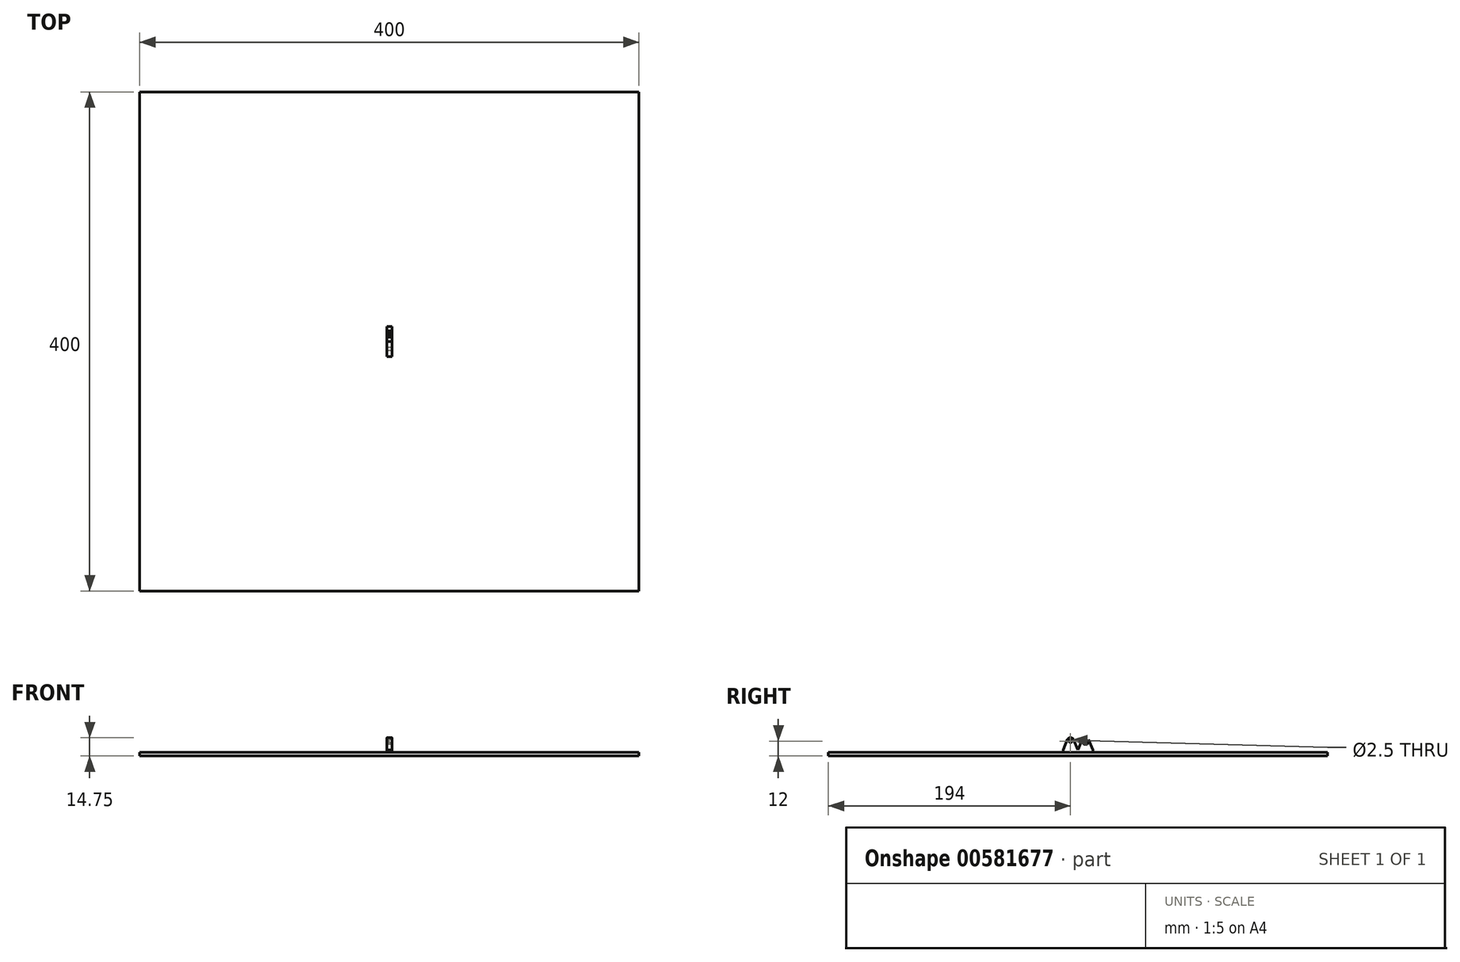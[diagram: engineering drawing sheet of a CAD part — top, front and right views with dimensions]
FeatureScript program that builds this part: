
annotation { "Feature Type Name" : "Feature", "Feature Type Description" : "" }
export const myFeature = defineFeature(function(context is Context, id is Id, definition is map)
    precondition{}
    {
        {
            var Q0;
            Q0=qCreatedBy(makeId("Top.planeOp"),FACE);
            var sketch = newSketch(context, id + "F0", { "sketchPlane" : qUnion([Q0])});
            skLineSegment(sketch, "E0.bottom", {"start": v(-200, -200) * mm, "end": v(200, -200) * mm});
            skLineSegment(sketch, "E0.top", {"start": v(-200, 200) * mm, "end": v(200, 200) * mm});
            skLineSegment(sketch, "E0.left", {"start": v(-200, -200) * mm, "end": v(-200, 200) * mm});
            skLineSegment(sketch, "E0.right", {"start": v(200, -200) * mm, "end": v(200, 200) * mm});
            skPoint(sketch, "E1.firstSnap0", {"position": v(-200, 0) * mm});
            skSolve(sketch);
        }
        {
            var Q0;
            Q0=makeQuery(id+"F0.imprint","IMPRINT",FACE,{"disambiguationData":[TD([[makeQuery(id+"F0.imprint","IMPRINT",EDGE,{"derivedFrom":sQuery(id+"F0.wireOp",EDGE,"E0.bottom")}),1.0]])]});
            extrude(context, id + "F1", {"entities" : qUnion([Q0]), "oppositeDirection" : true, "depth" : 3 * mm, "offsetDistance" : 25 * mm});
        }
        {
            var Q0;
            Q0=qCreatedBy(makeId("Right.planeOp"),FACE);
            var sketch = newSketch(context, id + "F2", { "sketchPlane" : qUnion([Q0])});
            skLineSegment(sketch, "E2.bottom", {"start": v(-12, 0) * mm, "end": v(0, 0) * mm});
            skLineSegment(sketch, "E2.top", {"start": v(-12, 2) * mm, "end": v(0, 2) * mm});
            skLineSegment(sketch, "E2.left", {"start": v(-12, 0) * mm, "end": v(-12, 2) * mm});
            skLineSegment(sketch, "E2.right", {"start": v(0, 0) * mm, "end": v(0, 2) * mm});
            skCircle(sketch, "E3", {"center": v(-6, 9) * mm, "radius": 1.25 * mm});
            skCircle(sketch, "E4", {"center": v(-6, 9) * mm, "radius": 2.75 * mm});
            skLineSegment(sketch, "E5", {"start": v(-12, 2) * mm, "end": v(-8.53, 10.09) * mm});
            skLineSegment(sketch, "E6", {"start": v(0, 2) * mm, "end": v(-3.47, 10.09) * mm});
            skLineSegment(sketch, "E7.MirrorCS", {"start": v(12, 2) * mm, "end": v(8.53, 10.09) * mm});
            skCircle(sketch, "E8.MirrorC", {"center": v(6, 9) * mm, "radius": 2.75 * mm});
            skLineSegment(sketch, "E9.MirrorCS", {"start": v(0, 2) * mm, "end": v(3.47, 10.09) * mm});
            skCircle(sketch, "E10.MirrorC", {"center": v(6, 9) * mm, "radius": 1.25 * mm});
            skLineSegment(sketch, "E11.MirrorCS", {"start": v(12, 0) * mm, "end": v(12, 2) * mm});
            skLineSegment(sketch, "E12.MirrorCS", {"start": v(12, 0) * mm, "end": v(0, 0) * mm});
            skLineSegment(sketch, "E13.MirrorCS", {"start": v(12, 2) * mm, "end": v(0, 2) * mm});
            skSolve(sketch);
        }
        {
            var Q0;
            Q0=makeQuery(id+"F2.imprint","IMPRINT",FACE,{"disambiguationData":[TD([[makeQuery(id+"F2.imprint","IMPRINT",EDGE,{"derivedFrom":sQuery(id+"F2.wireOp",EDGE,"E3")}),-1.0]])]});
            var Q1;
            Q1=makeQuery(id+"F2.imprint","IMPRINT",FACE,{"disambiguationData":[TD([[makeQuery(id+"F2.imprint","IMPRINT",EDGE,{"derivedFrom":sQuery(id+"F2.wireOp",EDGE,"E2.top")}),1.0]])]});
            var Q2;
            Q2=makeQuery(id+"F2.imprint","IMPRINT",FACE,{"disambiguationData":[TD([[makeQuery(id+"F2.imprint","IMPRINT",EDGE,{"derivedFrom":sQuery(id+"F2.wireOp",EDGE,"E2.bottom")}),1.0]])]});
            var Q3;
            Q3=makeQuery(id+"F2.imprint","IMPRINT",FACE,{"disambiguationData":[TD([[makeQuery(id+"F2.imprint","IMPRINT",EDGE,{"derivedFrom":sQuery(id+"F2.wireOp",EDGE,"E2.right")}),-1.0]])]});
            var Q4;
            {var subQ0=sQuery(id+"F2.wireOp",EDGE,"E7.MirrorCS");Q4=makeQuery(id+"F2.imprint","IMPRINT",FACE,{"disambiguationData":[TD([[makeQuery(id+"F2.imprint","IMPRINT",EDGE,{"derivedFrom":subQ0}),1.0]])]});}
            var Q5;
            Q5=makeQuery(id+"F2.imprint","IMPRINT",FACE,{"disambiguationData":[TD([[makeQuery(id+"F2.imprint","IMPRINT",EDGE,{"derivedFrom":sQuery(id+"F2.wireOp",EDGE,"E10.MirrorC")}),1.0]])]});
            extrude(context, id + "F3", {"entities" : qUnion([Q0, Q1, Q2, Q3, Q4, Q5]), "operationType" : NewBodyOperationType.ADD, "depth" : 2 * mm, "offsetDistance" : 25 * mm});
        }
        {
            var Q0;
            Q0=makeQuery(id+"F3.opExtrude","CAP_FACE",FACE,{"disambiguationData":[OSD([sQuery(id+"F2.wireOp",EDGE,"E2.bottom"),sQuery(id+"F2.wireOp",EDGE,"E2.left"),sQuery(id+"F2.wireOp",EDGE,"E3"),sQuery(id+"F2.wireOp",EDGE,"E4"),sQuery(id+"F2.wireOp",EDGE,"E5"),sQuery(id+"F2.wireOp",EDGE,"E6"),sQuery(id+"F2.wireOp",EDGE,"E7.MirrorCS"),sQuery(id+"F2.wireOp",EDGE,"E8.MirrorC"),sQuery(id+"F2.wireOp",EDGE,"E9.MirrorCS"),sQuery(id+"F2.wireOp",EDGE,"E10.MirrorC"),sQuery(id+"F2.wireOp",EDGE,"E11.MirrorCS"),sQuery(id+"F2.wireOp",EDGE,"E12.MirrorCS")])],"isStart":true});
            extrude(context, id + "F4", {"entities" : qUnion([Q0]), "operationType" : NewBodyOperationType.ADD, "depth" : 2 * mm, "offsetDistance" : 25 * mm});
        }
    });
